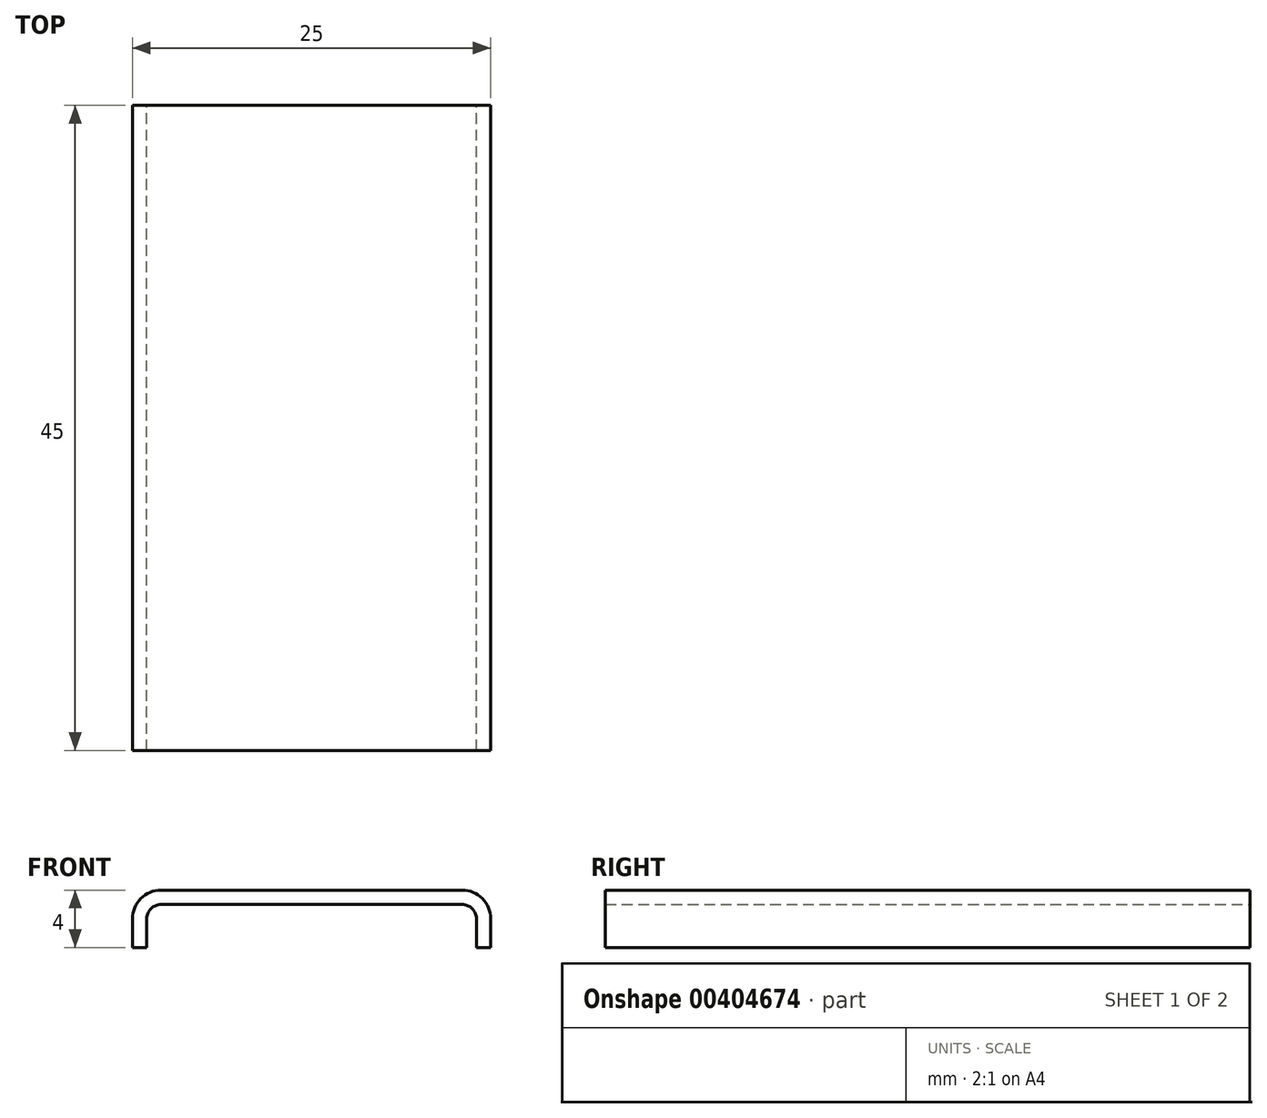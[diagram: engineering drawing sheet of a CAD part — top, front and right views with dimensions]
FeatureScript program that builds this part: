
annotation { "Feature Type Name" : "Feature", "Feature Type Description" : "" }
export const myFeature = defineFeature(function(context is Context, id is Id, definition is map)
    precondition{}
    {
        {
            var Q0;
            Q0=qCreatedBy(makeId("Front.planeOp"),FACE);
            var sketch = newSketch(context, id + "F0", { "sketchPlane" : qUnion([Q0])});
            skLineSegment(sketch, "E0.top", {"start": v(10.5, 2) * mm, "end": v(-10.5, 2) * mm});
            skLineSegment(sketch, "E0.left", {"start": v(12.5, -2) * mm, "end": v(12.5, 0) * mm});
            skLineSegment(sketch, "E0.right", {"start": v(-12.5, -2) * mm, "end": v(-12.5, 0) * mm});
            skPoint(sketch, "E0.middle", {"position": v(0, 0) * mm});
            skLineSegment(sketch, "E1", {"start": v(-12.5, -2) * mm, "end": v(-11.5, -2) * mm});
            skLineSegment(sketch, "E2", {"start": v(-11.5, -2) * mm, "end": v(-11.5, 0) * mm});
            skLineSegment(sketch, "E3", {"start": v(-10.5, 1) * mm, "end": v(10.5, 1) * mm});
            skLineSegment(sketch, "E4", {"start": v(11.5, 0) * mm, "end": v(11.5, -2) * mm});
            skLineSegment(sketch, "E5", {"start": v(11.5, -2) * mm, "end": v(12.5, -2) * mm});
            skPoint(sketch, "E6.visualSharp", {"position": v(-11.5, 1) * mm});
            skArc(sketch, "E6.filletArc", {"start": v(-10.5, 1) * mm, "mid": v(-11.2, 0.7) * mm, "end": v(-11.5, 0) * mm});
            skPoint(sketch, "E7.visualSharp", {"position": v(11.5, 1) * mm});
            skArc(sketch, "E7.filletArc", {"start": v(11.5, 0) * mm, "mid": v(11.2, 0.7) * mm, "end": v(10.5, 1) * mm});
            skPoint(sketch, "E8.visualSharp", {"position": v(-12.5, 2) * mm});
            skArc(sketch, "E8.filletArc", {"start": v(-10.5, 2) * mm, "mid": v(-11.91, 1.41) * mm, "end": v(-12.5, 0) * mm});
            skPoint(sketch, "E9.visualSharp", {"position": v(12.5, 2) * mm});
            skArc(sketch, "E9.filletArc", {"start": v(12.5, 0) * mm, "mid": v(11.91, 1.41) * mm, "end": v(10.5, 2) * mm});
            skSolve(sketch);
        }
        {
            var Q0;
            Q0 = qSketchRegion(id + "F0", true);
            extrude(context, id + "F1", {"entities" : qUnion([Q0]), "depth" : 45 * mm});
        }
    });
